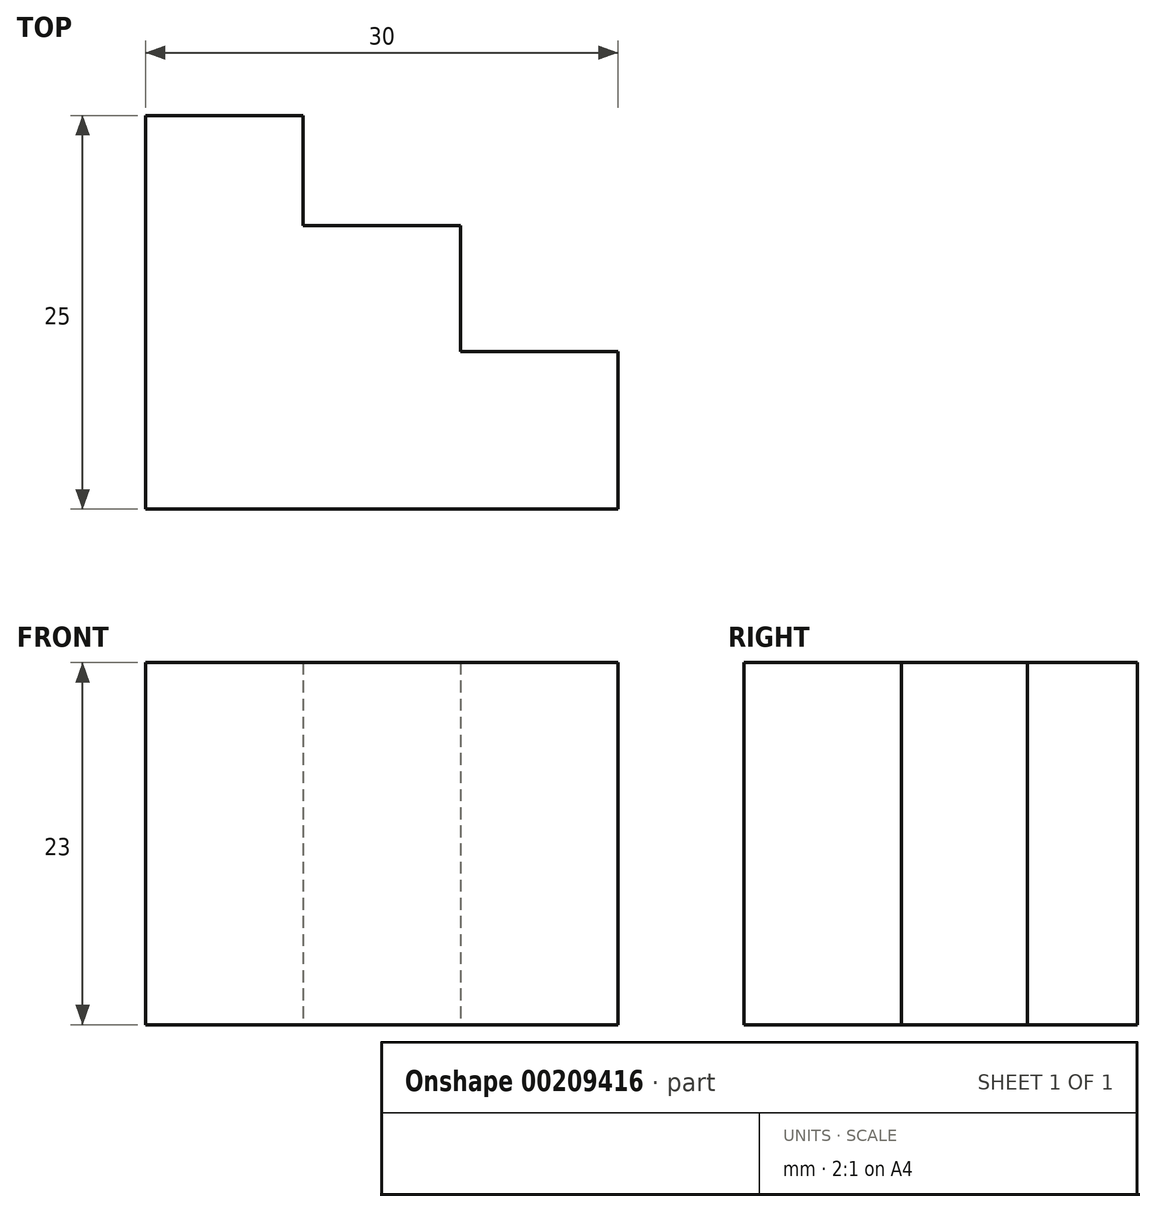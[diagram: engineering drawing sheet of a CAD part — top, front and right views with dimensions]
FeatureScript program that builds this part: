
annotation { "Feature Type Name" : "Feature", "Feature Type Description" : "" }
export const myFeature = defineFeature(function(context is Context, id is Id, definition is map)
    precondition{}
    {
        {
            var Q0;
            Q0=qCreatedBy(makeId("Top.planeOp"),FACE);
            var sketch = newSketch(context, id + "F0", { "sketchPlane" : qUnion([Q0])});
            skLineSegment(sketch, "E0.left", {"start": v(0, 0) * mm, "end": v(0, 25) * mm});
            skLineSegment(sketch, "E1", {"start": v(0, 0) * mm, "end": v(30, 0) * mm});
            skLineSegment(sketch, "E2", {"start": v(30, 0) * mm, "end": v(30, 10) * mm});
            skLineSegment(sketch, "E3", {"start": v(30, 10) * mm, "end": v(20, 10) * mm});
            skLineSegment(sketch, "E4", {"start": v(20, 10) * mm, "end": v(20, 18) * mm});
            skLineSegment(sketch, "E5", {"start": v(20, 18) * mm, "end": v(10, 18) * mm});
            skLineSegment(sketch, "E6", {"start": v(10, 18) * mm, "end": v(10, 25) * mm});
            skLineSegment(sketch, "E7", {"start": v(10, 25) * mm, "end": v(0, 25) * mm});
            skSolve(sketch);
        }
        {
            var Q0;
            Q0=makeQuery(id+"F0.imprint","IMPRINT",FACE,{"disambiguationData":[TD([[makeQuery(id+"F0.imprint","IMPRINT",EDGE,{"derivedFrom":sQuery(id+"F0.wireOp",EDGE,"E0.left")}),-1.0]])]});
            extrude(context, id + "F1", {"entities" : qUnion([Q0]), "depth" : 23 * mm});
        }
    });
